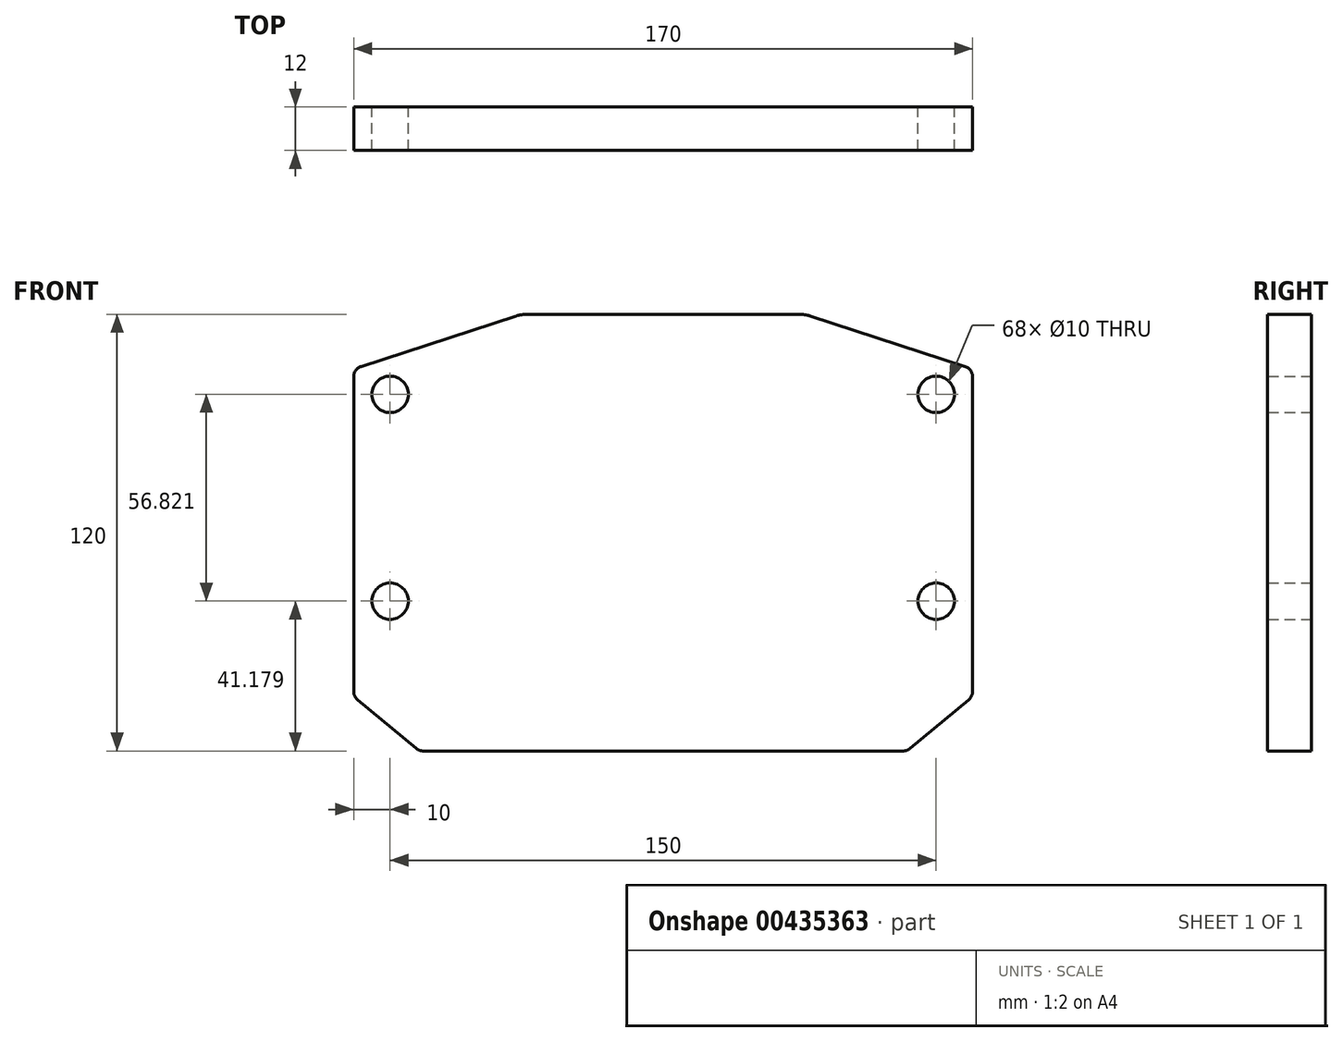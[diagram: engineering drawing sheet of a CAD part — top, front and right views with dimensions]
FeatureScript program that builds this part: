
annotation { "Feature Type Name" : "Feature", "Feature Type Description" : "" }
export const myFeature = defineFeature(function(context is Context, id is Id, definition is map)
    precondition{}
    {
        {
            var Q0;
            Q0=qCreatedBy(makeId("Front.planeOp"),FACE);
            var sketch = newSketch(context, id + "F0", { "sketchPlane" : qUnion([Q0])});
            skLineSegment(sketch, "E0", {"start": v(85, -81.6) * mm, "end": v(85, 4.82) * mm});
            skLineSegment(sketch, "E1", {"start": v(82.93, 7.67) * mm, "end": v(40.51, 21.5) * mm});
            skLineSegment(sketch, "E2", {"start": v(83.92, -83.9) * mm, "end": v(67.83, -97.3) * mm});
            skLineSegment(sketch, "E3", {"start": v(85, 7) * mm, "end": v(85, -63) * mm});
            skLineSegment(sketch, "E4", {"start": v(39.76, 16.75) * mm, "end": v(76.55, 4.75) * mm});
            skLineSegment(sketch, "E5", {"start": v(85, 2) * mm, "end": v(85, 7) * mm});
            skLineSegment(sketch, "E6", {"start": v(80, 0) * mm, "end": v(80, -56.82) * mm});
            skLineSegment(sketch, "E7", {"start": v(77.24, -61.3) * mm, "end": v(24.88, -87.47) * mm});
            skLineSegment(sketch, "E8", {"start": v(0, -88.53) * mm, "end": v(0, -88) * mm});
            skPoint(sketch, "E8.endSnap0", {"position": v(0, -88.53) * mm});
            skLineSegment(sketch, "E9", {"start": v(0, -88) * mm, "end": v(22.64, -88) * mm});
            skPoint(sketch, "E10.orphan", {"position": v(22.76, -88.53) * mm});
            skPoint(sketch, "E11.visualSharp", {"position": v(80, 3.63) * mm});
            skArc(sketch, "E11.filletArc", {"start": v(80, 0) * mm, "mid": v(79.05, 2.94) * mm, "end": v(76.55, 4.75) * mm});
            skPoint(sketch, "E12.visualSharp", {"position": v(80, -59.91) * mm});
            skArc(sketch, "E12.filletArc", {"start": v(77.24, -61.3) * mm, "mid": v(79.25, -59.45) * mm, "end": v(80, -56.82) * mm});
            skPoint(sketch, "E13.visualSharp", {"position": v(23.82, -88) * mm});
            skArc(sketch, "E13.filletArc", {"start": v(22.64, -88) * mm, "mid": v(23.79, -87.87) * mm, "end": v(24.88, -87.47) * mm});
            skPoint(sketch, "E14.visualSharp", {"position": v(39, 17) * mm});
            skArc(sketch, "E14.filletArc", {"start": v(39.76, 16.75) * mm, "mid": v(39, 16.94) * mm, "end": v(38.2, 17) * mm});
            skLineSegment(sketch, "E15", {"start": v(40.51, 21.5) * mm, "end": v(62, 14.5) * mm});
            skLineSegment(sketch, "E16", {"start": v(62, 14.5) * mm, "end": v(71.5, 11.4) * mm});
            skLineSegment(sketch, "E17", {"start": v(71.5, 11.4) * mm, "end": v(52.5, 17.6) * mm});
            skPoint(sketch, "E18.visualSharp", {"position": v(67, -98) * mm});
            skArc(sketch, "E18.filletArc", {"start": v(65.91, -98) * mm, "mid": v(66.94, -97.82) * mm, "end": v(67.83, -97.3) * mm});
            skPoint(sketch, "E19.visualSharp", {"position": v(85, -83) * mm});
            skArc(sketch, "E19.filletArc", {"start": v(83.92, -83.9) * mm, "mid": v(84.72, -82.87) * mm, "end": v(85, -81.6) * mm});
            skLineSegment(sketch, "E20", {"start": v(85, 7) * mm, "end": v(85, -23) * mm});
            skLineSegment(sketch, "E21", {"start": v(85, -23) * mm, "end": v(85, -43) * mm});
            skLineSegment(sketch, "E22", {"start": v(90, -26) * mm, "end": v(90, -40) * mm});
            skPoint(sketch, "E23.visualSharp", {"position": v(39, 22) * mm});
            skPoint(sketch, "E24.visualSharp", {"position": v(85, 7) * mm});
            skArc(sketch, "E24.filletArc", {"start": v(85, 4.82) * mm, "mid": v(84.43, 6.58) * mm, "end": v(82.93, 7.67) * mm});
            skPoint(sketch, "E25.visualSharp", {"position": v(117, -81.6) * mm});
            skPoint(sketch, "E26.newPointA", {"position": v(90, -43) * mm});
            skPoint(sketch, "E26.newPointB", {"position": v(85, -43) * mm});
            skArc(sketch, "E26.filletArc", {"start": v(90, -40) * mm, "mid": v(90.88, -42.12) * mm, "end": v(93, -43) * mm});
            skPoint(sketch, "E27.visualSharp", {"position": v(90, -23) * mm});
            skArc(sketch, "E27.filletArc", {"start": v(93, -23) * mm, "mid": v(90.88, -23.88) * mm, "end": v(90, -26) * mm});
            skPoint(sketch, "E28.visualSharp", {"position": v(117, 4.82) * mm});
            skPoint(sketch, "E29.visualSharp", {"position": v(65.91, -130) * mm});
            skArc(sketch, "E29.filletArc", {"start": v(62.91, -130) * mm, "mid": v(65.04, -129.12) * mm, "end": v(65.91, -127) * mm});
            skArc(sketch, "E30.filletArc", {"start": v(40.51, 21.5) * mm, "mid": v(38.98, 21.87) * mm, "end": v(37.41, 22) * mm});
            skPoint(sketch, "E31.visualSharp", {"position": v(37.41, 54) * mm});
            skArc(sketch, "E31.filletArc", {"start": v(37.41, 51) * mm, "mid": v(36.53, 53.12) * mm, "end": v(34.41, 54) * mm});
            skLineSegment(sketch, "E32", {"start": v(39, 17) * mm, "end": v(38.2, 12) * mm});
            skLineSegment(sketch, "E33", {"start": v(80, 3.63) * mm, "end": v(75, 0) * mm});
            skLineSegment(sketch, "E34", {"start": v(80, -59.91) * mm, "end": v(75, -56.82) * mm});
            skLineSegment(sketch, "E35", {"start": v(23.82, -88) * mm, "end": v(22.64, -83) * mm});
            skLineSegment(sketch, "E36", {"start": v(114, 4.82) * mm, "end": v(117, 4.82) * mm});
            skLineSegment(sketch, "E37", {"start": v(117, 4.82) * mm, "end": v(119, 4.82) * mm});
            skLineSegment(sketch, "E38", {"start": v(122, 1.82) * mm, "end": v(122, -78.6) * mm});
            skLineSegment(sketch, "E39", {"start": v(119, -81.6) * mm, "end": v(117, -81.6) * mm});
            skLineSegment(sketch, "E40", {"start": v(114, -81.6) * mm, "end": v(117, -81.6) * mm});
            skPoint(sketch, "E41.visualSharp", {"position": v(122, 4.82) * mm});
            skArc(sketch, "E41.filletArc", {"start": v(122, 1.82) * mm, "mid": v(121.12, 3.94) * mm, "end": v(119, 4.82) * mm});
            skPoint(sketch, "E42.visualSharp", {"position": v(122, -81.6) * mm});
            skArc(sketch, "E42.filletArc", {"start": v(119, -81.6) * mm, "mid": v(121.12, -80.72) * mm, "end": v(122, -78.6) * mm});
            skLineSegment(sketch, "E43", {"start": v(80, -56.82) * mm, "end": v(75, -56.82) * mm});
            skLineSegment(sketch, "E44", {"start": v(80, 0) * mm, "end": v(75, 0) * mm});
            skLineSegment(sketch, "E45", {"start": v(90, -33) * mm, "end": v(118, -33) * mm});
            skLineSegment(sketch, "E46", {"start": v(118, -33) * mm, "end": v(118, -26) * mm});
            skLineSegment(sketch, "E47", {"start": v(115, -23) * mm, "end": v(93, -23) * mm});
            skLineSegment(sketch, "E48", {"start": v(93, -43) * mm, "end": v(115, -43) * mm});
            skLineSegment(sketch, "E49", {"start": v(118, -40) * mm, "end": v(118, -33) * mm});
            skPoint(sketch, "E50.visualSharp", {"position": v(118, -23) * mm});
            skArc(sketch, "E50.filletArc", {"start": v(118, -26) * mm, "mid": v(117.12, -23.88) * mm, "end": v(115, -23) * mm});
            skPoint(sketch, "E51.visualSharp", {"position": v(118, -43) * mm});
            skArc(sketch, "E51.filletArc", {"start": v(115, -43) * mm, "mid": v(117.12, -42.12) * mm, "end": v(118, -40) * mm});
            skLineSegment(sketch, "E52", {"start": v(54.04, 22.35) * mm, "end": v(61.8, 46.12) * mm});
            skLineSegment(sketch, "E53", {"start": v(65.58, 48.04) * mm, "end": v(78.89, 43.7) * mm});
            skLineSegment(sketch, "E54", {"start": v(80.8, 39.92) * mm, "end": v(73.06, 16.15) * mm});
            skPoint(sketch, "E55.visualSharp", {"position": v(62.72, 48.97) * mm});
            skArc(sketch, "E55.filletArc", {"start": v(65.58, 48.04) * mm, "mid": v(63.29, 47.86) * mm, "end": v(61.8, 46.12) * mm});
            skPoint(sketch, "E56.visualSharp", {"position": v(81.74, 42.77) * mm});
            skArc(sketch, "E56.filletArc", {"start": v(80.8, 39.92) * mm, "mid": v(80.63, 42.2) * mm, "end": v(78.89, 43.7) * mm});
            skLineSegment(sketch, "E57", {"start": v(63.55, 19.25) * mm, "end": v(73.06, 16.15) * mm});
            skLineSegment(sketch, "E58", {"start": v(73.06, 16.15) * mm, "end": v(54.04, 22.35) * mm});
            skLineSegment(sketch, "E59", {"start": v(54.83, 55.75) * mm, "end": v(91.55, 43.78) * mm});
            skPoint(sketch, "E60.visualSharp", {"position": v(94.4, 42.85) * mm});
            skArc(sketch, "E60.filletArc", {"start": v(93.47, 40) * mm, "mid": v(93.3, 42.29) * mm, "end": v(91.55, 43.78) * mm});
            skPoint(sketch, "E61.visualSharp", {"position": v(51.98, 56.68) * mm});
            skArc(sketch, "E61.filletArc", {"start": v(54.83, 55.75) * mm, "mid": v(52.54, 55.57) * mm, "end": v(51.05, 53.83) * mm});
            skLineSegment(sketch, "E62", {"start": v(34.41, 54) * mm, "end": v(0, 54) * mm});
            skLineSegment(sketch, "E63", {"start": v(62.91, -130) * mm, "end": v(0, -130) * mm});
            skPoint(sketch, "E64.orphan", {"position": v(0, 0) * mm});
            skLineSegment(sketch, "E65", {"start": v(38.2, 17) * mm, "end": v(0, 17) * mm});
            skArc(sketch, "E66.MirrorCS", {"start": v(-39.76, 16.75) * mm, "mid": v(-39, 16.94) * mm, "end": v(-38.2, 17) * mm});
            skArc(sketch, "E67.MirrorCS", {"start": v(-40.51, 21.5) * mm, "mid": v(-38.98, 21.87) * mm, "end": v(-37.41, 22) * mm});
            skArc(sketch, "E68.MirrorCS", {"start": v(-83.92, -83.9) * mm, "mid": v(-84.72, -82.87) * mm, "end": v(-85, -81.6) * mm});
            skLineSegment(sketch, "E69.MirrorCS", {"start": v(-39, 17) * mm, "end": v(-38.2, 12) * mm});
            skArc(sketch, "E70.MirrorCS", {"start": v(-85, 4.82) * mm, "mid": v(-84.43, 6.58) * mm, "end": v(-82.93, 7.67) * mm});
            skArc(sketch, "E71.MirrorCS", {"start": v(-22.64, -88) * mm, "mid": v(-23.79, -87.87) * mm, "end": v(-24.88, -87.47) * mm});
            skLineSegment(sketch, "E72.MirrorCS", {"start": v(-85, 2) * mm, "end": v(-85, 7) * mm});
            skLineSegment(sketch, "E73.MirrorCS", {"start": v(-23.82, -88) * mm, "end": v(-22.64, -83) * mm});
            skArc(sketch, "E74.MirrorCS", {"start": v(-77.24, -61.3) * mm, "mid": v(-79.25, -59.45) * mm, "end": v(-80, -56.82) * mm});
            skLineSegment(sketch, "E75.MirrorCS", {"start": v(-80, -59.91) * mm, "end": v(-75, -56.82) * mm});
            skLineSegment(sketch, "E76.MirrorCS", {"start": v(-80, -56.82) * mm, "end": v(-75, -56.82) * mm});
            skArc(sketch, "E77.MirrorCS", {"start": v(-80, 0) * mm, "mid": v(-79.05, 2.94) * mm, "end": v(-76.55, 4.75) * mm});
            skLineSegment(sketch, "E78.MirrorCS", {"start": v(-80, 3.63) * mm, "end": v(-75, 0) * mm});
            skArc(sketch, "E79.MirrorCS", {"start": v(-65.91, -98) * mm, "mid": v(-66.94, -97.82) * mm, "end": v(-67.83, -97.3) * mm});
            skLineSegment(sketch, "E80.MirrorCS", {"start": v(-80, 0) * mm, "end": v(-75, 0) * mm});
            skLineSegment(sketch, "E81.MirrorCS", {"start": v(-119, -81.6) * mm, "end": v(-117, -81.6) * mm});
            skArc(sketch, "E82.MirrorCS", {"start": v(-62.91, -130) * mm, "mid": v(-65.04, -129.12) * mm, "end": v(-65.91, -127) * mm});
            skLineSegment(sketch, "E83.MirrorCS", {"start": v(-118, -33) * mm, "end": v(-118, -26) * mm});
            skArc(sketch, "E84.MirrorCS", {"start": v(-65.58, 48.04) * mm, "mid": v(-63.29, 47.86) * mm, "end": v(-61.8, 46.12) * mm});
            skLineSegment(sketch, "E85.MirrorCS", {"start": v(-114, -81.6) * mm, "end": v(-117, -81.6) * mm});
            skLineSegment(sketch, "E86.MirrorCS", {"start": v(-117, 4.82) * mm, "end": v(-119, 4.82) * mm});
            skLineSegment(sketch, "E87.MirrorCS", {"start": v(-62, 14.5) * mm, "end": v(-71.5, 11.4) * mm});
            skArc(sketch, "E88.MirrorCS", {"start": v(-80.8, 39.92) * mm, "mid": v(-80.63, 42.2) * mm, "end": v(-78.89, 43.7) * mm});
            skArc(sketch, "E89.MirrorCS", {"start": v(-118, -26) * mm, "mid": v(-117.12, -23.88) * mm, "end": v(-115, -23) * mm});
            skLineSegment(sketch, "E90.MirrorCS", {"start": v(-118, -40) * mm, "end": v(-118, -33) * mm});
            skLineSegment(sketch, "E91.MirrorCS", {"start": v(-40.51, 21.5) * mm, "end": v(-62, 14.5) * mm});
            skArc(sketch, "E92.MirrorCS", {"start": v(-122, 1.82) * mm, "mid": v(-121.12, 3.94) * mm, "end": v(-119, 4.82) * mm});
            skArc(sketch, "E93.MirrorCS", {"start": v(-115, -43) * mm, "mid": v(-117.12, -42.12) * mm, "end": v(-118, -40) * mm});
            skArc(sketch, "E94.MirrorCS", {"start": v(-54.83, 55.75) * mm, "mid": v(-52.54, 55.57) * mm, "end": v(-51.05, 53.83) * mm});
            skArc(sketch, "E95.MirrorCS", {"start": v(-93.47, 40) * mm, "mid": v(-93.3, 42.29) * mm, "end": v(-91.55, 43.78) * mm});
            skArc(sketch, "E96.MirrorCS", {"start": v(-119, -81.6) * mm, "mid": v(-121.12, -80.72) * mm, "end": v(-122, -78.6) * mm});
            skArc(sketch, "E97.MirrorCS", {"start": v(-90, -40) * mm, "mid": v(-90.88, -42.12) * mm, "end": v(-93, -43) * mm});
            skArc(sketch, "E98.MirrorCS", {"start": v(-37.41, 51) * mm, "mid": v(-36.53, 53.12) * mm, "end": v(-34.41, 54) * mm});
            skLineSegment(sketch, "E99.MirrorCS", {"start": v(-82.93, 7.67) * mm, "end": v(-40.51, 21.5) * mm});
            skLineSegment(sketch, "E100.MirrorCS", {"start": v(-85, -23) * mm, "end": v(-85, -43) * mm});
            skArc(sketch, "E101.MirrorCS", {"start": v(-93, -23) * mm, "mid": v(-90.88, -23.88) * mm, "end": v(-90, -26) * mm});
            skLineSegment(sketch, "E102.MirrorCS", {"start": v(-71.5, 11.4) * mm, "end": v(-52.5, 17.6) * mm});
            skLineSegment(sketch, "E103.MirrorCS", {"start": v(-90, -26) * mm, "end": v(-90, -40) * mm});
            skPoint(sketch, "E104.MirrorP", {"position": v(-39, 22) * mm});
            skPoint(sketch, "E105.MirrorP", {"position": v(-39, 17) * mm});
            skLineSegment(sketch, "E106.MirrorCS", {"start": v(-90, -33) * mm, "end": v(-118, -33) * mm});
            skLineSegment(sketch, "E107.MirrorCS", {"start": v(-85, 7) * mm, "end": v(-85, -23) * mm});
            skPoint(sketch, "E108.MirrorP", {"position": v(-22.76, -88.53) * mm});
            skLineSegment(sketch, "E109.MirrorCS", {"start": v(-83.92, -83.9) * mm, "end": v(-67.83, -97.3) * mm});
            skLineSegment(sketch, "E110.MirrorCS", {"start": v(-85, -81.6) * mm, "end": v(-85, 4.82) * mm});
            skPoint(sketch, "E111.MirrorP", {"position": v(-118, -43) * mm});
            skLineSegment(sketch, "E112.MirrorCS", {"start": v(-80, 0) * mm, "end": v(-80, -56.82) * mm});
            skPoint(sketch, "E113.MirrorP", {"position": v(-94.4, 42.85) * mm});
            skLineSegment(sketch, "E114.MirrorCS", {"start": v(-122, 1.82) * mm, "end": v(-122, -78.6) * mm});
            skPoint(sketch, "E115.MirrorP", {"position": v(-117, -81.6) * mm});
            skPoint(sketch, "E116.MirrorP", {"position": v(-90, -23) * mm});
            skPoint(sketch, "E117.MirrorP", {"position": v(-90, -43) * mm});
            skLineSegment(sketch, "E118.MirrorCS", {"start": v(-85, 7) * mm, "end": v(-85, -63) * mm});
            skPoint(sketch, "E119.MirrorP", {"position": v(-67, -98) * mm});
            skPoint(sketch, "E120.MirrorP", {"position": v(-122, -81.6) * mm});
            skPoint(sketch, "E121.MirrorP", {"position": v(-80, -59.91) * mm});
            skPoint(sketch, "E122.MirrorP", {"position": v(-85, -83) * mm});
            skPoint(sketch, "E123.MirrorP", {"position": v(-81.74, 42.77) * mm});
            skPoint(sketch, "E124.MirrorP", {"position": v(-65.91, -130) * mm});
            skPoint(sketch, "E125.MirrorP", {"position": v(-118, -23) * mm});
            skLineSegment(sketch, "E126.MirrorCS", {"start": v(-93, -43) * mm, "end": v(-115, -43) * mm});
            skLineSegment(sketch, "E127.MirrorCS", {"start": v(-39.76, 16.75) * mm, "end": v(-76.55, 4.75) * mm});
            skPoint(sketch, "E128.MirrorP", {"position": v(-117, 4.82) * mm});
            skLineSegment(sketch, "E129.MirrorCS", {"start": v(-38.2, 17) * mm, "end": v(0, 17) * mm});
            skLineSegment(sketch, "E130.MirrorCS", {"start": v(-62.91, -130) * mm, "end": v(0, -130) * mm});
            skLineSegment(sketch, "E131.MirrorCS", {"start": v(-34.41, 54) * mm, "end": v(0, 54) * mm});
            skPoint(sketch, "E132.MirrorP", {"position": v(-85, 7) * mm});
            skPoint(sketch, "E133.MirrorP", {"position": v(-62.72, 48.97) * mm});
            skPoint(sketch, "E134.MirrorP", {"position": v(-85, -43) * mm});
            skPoint(sketch, "E135.MirrorP", {"position": v(-37.41, 54) * mm});
            skLineSegment(sketch, "E136.MirrorCS", {"start": v(-77.24, -61.3) * mm, "end": v(-24.88, -87.47) * mm});
            skPoint(sketch, "E137.MirrorP", {"position": v(-51.98, 56.68) * mm});
            skPoint(sketch, "E138.MirrorP", {"position": v(-23.82, -88) * mm});
            skPoint(sketch, "E139.MirrorP", {"position": v(-122, 4.82) * mm});
            skPoint(sketch, "E140.MirrorP", {"position": v(-80, 3.63) * mm});
            skLineSegment(sketch, "E141.MirrorCS", {"start": v(0, -88) * mm, "end": v(-22.64, -88) * mm});
            skPoint(sketch, "E142.orphan", {"position": v(85, -33) * mm});
            skPoint(sketch, "E143.start.orphan", {"position": v(37.41, 22) * mm});
            skLineSegment(sketch, "E144", {"start": v(-37.41, 22) * mm, "end": v(37.41, 22) * mm});
            skLineSegment(sketch, "E145", {"start": v(-65.91, -98) * mm, "end": v(65.91, -98) * mm});
            skCircle(sketch, "E146", {"center": v(-75, 0) * mm, "radius": 5 * mm});
            skCircle(sketch, "E147", {"center": v(-75, -56.82) * mm, "radius": 5 * mm});
            skCircle(sketch, "E148", {"center": v(75, -56.82) * mm, "radius": 5 * mm});
            skCircle(sketch, "E149", {"center": v(75, 0) * mm, "radius": 5 * mm});
            skSolve(sketch);
        }
        {
            var Q0;
            Q0=makeQuery(id+"F0.imprint","IMPRINT",FACE,{"disambiguationData":[TD([[makeQuery(id+"F0.imprint","IMPRINT",EDGE,{"derivedFrom":sQuery(id+"F0.wireOp",EDGE,"E0")}),1.0]])]});
            var Q1;
            {var subQ19=sQuery(id+"F0.wireOp",EDGE,"E4");Q1=makeQuery(id+"F0.imprint","IMPRINT",FACE,{"disambiguationData":[TD([[makeQuery(id+"F0.imprint","IMPRINT",EDGE,{"derivedFrom":subQ19}),-1.0]])]});}
            extrude(context, id + "F1", {"entities" : qUnion([Q0, Q1]), "depth" : 12 * mm, "offsetDistance" : 25 * mm});
        }
    });
